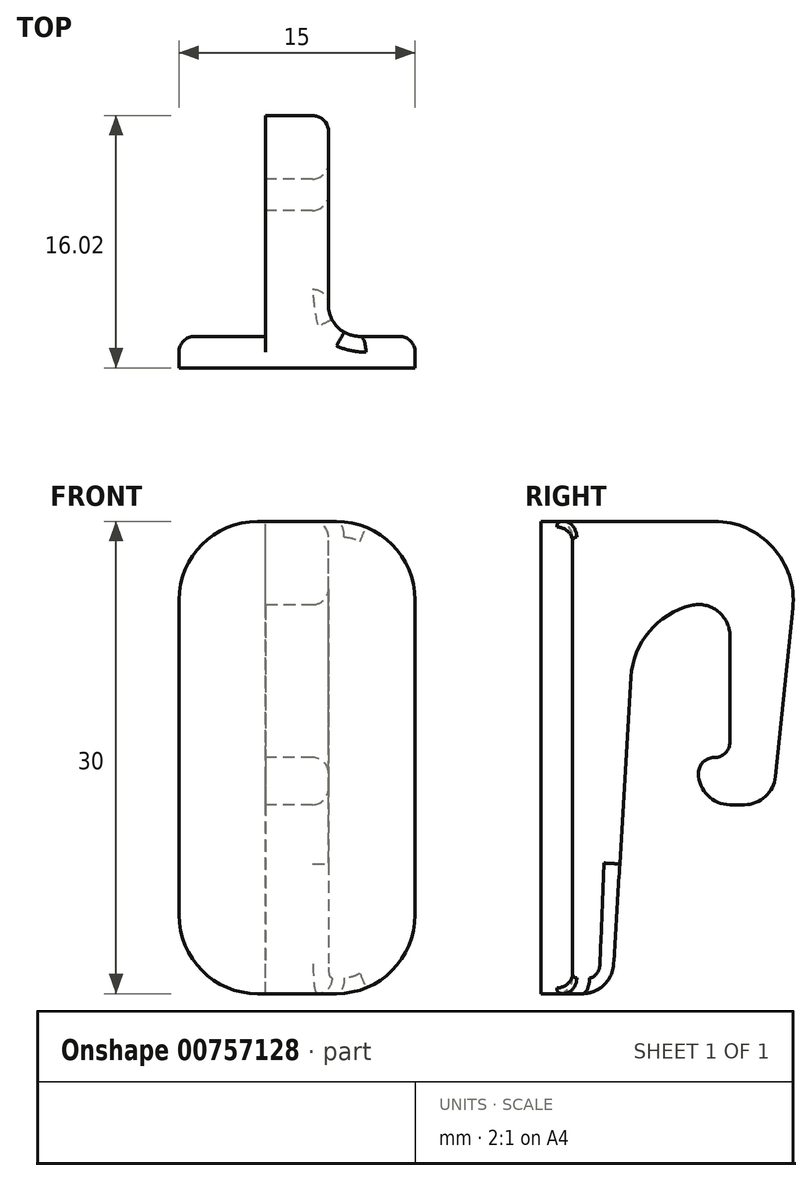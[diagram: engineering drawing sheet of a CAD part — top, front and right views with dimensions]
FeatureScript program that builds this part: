
annotation { "Feature Type Name" : "Feature", "Feature Type Description" : "" }
export const myFeature = defineFeature(function(context is Context, id is Id, definition is map)
    precondition{}
    {
        {
            var Q0;
            Q0=qCreatedBy(makeId("Right.planeOp"),FACE);
            var sketch = newSketch(context, id + "F0", { "sketchPlane" : qUnion([Q0])});
            skLineSegment(sketch, "E0", {"start": v(0, 0) * mm, "end": v(0, 30) * mm});
            skLineSegment(sketch, "E1", {"start": v(0, 30) * mm, "end": v(14.55, 30) * mm});
            skLineSegment(sketch, "E2", {"start": v(14.55, 30) * mm, "end": v(12.7, 12) * mm});
            skLineSegment(sketch, "E3", {"start": v(12.7, 12) * mm, "end": v(8, 12) * mm});
            skLineSegment(sketch, "E4", {"start": v(8, 12) * mm, "end": v(8, 15) * mm});
            skLineSegment(sketch, "E5", {"start": v(8, 15) * mm, "end": v(10, 15) * mm});
            skLineSegment(sketch, "E6", {"start": v(10, 15) * mm, "end": v(10, 24.8) * mm});
            skLineSegment(sketch, "E7", {"start": v(10, 24.8) * mm, "end": v(4, 24.8) * mm});
            skLineSegment(sketch, "E8", {"start": v(4, 24.8) * mm, "end": v(2.5, 0) * mm});
            skLineSegment(sketch, "E9", {"start": v(2.5, 0) * mm, "end": v(0, 0) * mm});
            skSolve(sketch);
        }
        {
            var Q0;
            Q0=makeQuery(id+"F0.imprint","IMPRINT",FACE,{"disambiguationData":[TD([[makeQuery(id+"F0.imprint","IMPRINT",EDGE,{"derivedFrom":sQuery(id+"F0.wireOp",EDGE,"E0")}),-1.0]])]});
            extrude(context, id + "F1", {"entities" : qUnion([Q0]), "endBound" : BoundingType.SYMMETRIC, "depth" : 4 * mm, "offsetDistance" : 25 * mm});
        }
        {
            var Q0;
            Q0=qCreatedBy(makeId("Front.planeOp"),FACE);
            var sketch = newSketch(context, id + "F2", { "sketchPlane" : qUnion([Q0])});
            skLineSegment(sketch, "E10.bottom", {"start": v(-7.5, 30) * mm, "end": v(7.5, 30) * mm});
            skLineSegment(sketch, "E10.top", {"start": v(-7.5, 0) * mm, "end": v(7.5, 0) * mm});
            skLineSegment(sketch, "E10.left", {"start": v(-7.5, 30) * mm, "end": v(-7.5, 0) * mm});
            skLineSegment(sketch, "E10.right", {"start": v(7.5, 30) * mm, "end": v(7.5, 0) * mm});
            skPoint(sketch, "E10.middle", {"position": v(0, 15) * mm});
            skSolve(sketch);
        }
        {
            var Q0;
            Q0 = qSketchRegion(id + "F2", true);
            extrude(context, id + "F3", {"entities" : qUnion([Q0]), "operationType" : NewBodyOperationType.ADD, "depth" : 2 * mm, "offsetDistance" : 25 * mm});
        }
        {
            var Q0;
            Q0=makeQuery(id+"F3.opExtrude","SWEPT_EDGE",EDGE,{"disambiguationData":[OSD([sQuery(id+"F2.wireOp",EDGE,"E10.bottom"),sQuery(id+"F2.wireOp",EDGE,"E10.right")])]});
            var Q1;
            Q1=makeQuery(id+"F3.opExtrude","SWEPT_EDGE",EDGE,{"disambiguationData":[OSD([sQuery(id+"F2.wireOp",EDGE,"E10.bottom"),sQuery(id+"F2.wireOp",EDGE,"E10.left")])]});
            var Q2;
            Q2=makeQuery(id+"F3.opExtrude","SWEPT_EDGE",EDGE,{"disambiguationData":[OSD([sQuery(id+"F2.wireOp",EDGE,"E10.top"),sQuery(id+"F2.wireOp",EDGE,"E10.right")])]});
            var Q3;
            Q3=makeQuery(id+"F1.opExtrude","SWEPT_EDGE",EDGE,{"disambiguationData":[OSD([sQuery(id+"F0.wireOp",EDGE,"E1"),sQuery(id+"F0.wireOp",EDGE,"E2")])]});
            var Q4;
            Q4=makeQuery(id+"F3.opExtrude","SWEPT_EDGE",EDGE,{"disambiguationData":[OSD([sQuery(id+"F2.wireOp",EDGE,"E10.top"),sQuery(id+"F2.wireOp",EDGE,"E10.left")])]});
            var Q5;
            Q5=makeQuery(id+"F1.opExtrude","SWEPT_EDGE",EDGE,{"disambiguationData":[OSD([sQuery(id+"F0.wireOp",EDGE,"E7"),sQuery(id+"F0.wireOp",EDGE,"E8")])]});
            fillet(context, id + "F4", {"entities" : qUnion([Q0, Q1, Q2, Q3, Q4, Q5]), "radius" : 5 * mm, "tangentPropagation" : true, "allowEdgeOverflow" : false});
        }
        {
            var Q0;
            Q0=makeQuery(id+"F1.opExtrude","SWEPT_EDGE",EDGE,{"disambiguationData":[OSD([sQuery(id+"F0.wireOp",EDGE,"E6"),sQuery(id+"F0.wireOp",EDGE,"E7")])]});
            var Q1;
            Q1=makeQuery(id+"F1.opExtrude","SWEPT_EDGE",EDGE,{"disambiguationData":[OSD([sQuery(id+"F0.wireOp",EDGE,"E3"),sQuery(id+"F0.wireOp",EDGE,"E4")])]});
            var Q2;
            Q2=makeQuery(id+"F1.opExtrude","SWEPT_EDGE",EDGE,{"disambiguationData":[OSD([sQuery(id+"F0.wireOp",EDGE,"E2"),sQuery(id+"F0.wireOp",EDGE,"E3")])]});
            var Q3;
            Q3=makeQuery(id+"F1.opExtrude","SWEPT_EDGE",EDGE,{"disambiguationData":[OSD([sQuery(id+"F0.wireOp",EDGE,"E8"),sQuery(id+"F0.wireOp",EDGE,"E9")])]});
            fillet(context, id + "F5", {"entities" : qUnion([Q0, Q1, Q2, Q3]), "radius" : 2 * mm, "tangentPropagation" : true, "allowEdgeOverflow" : false});
        }
        {
            var Q0;
            Q0=makeQuery(id+"F1.opExtrude","CAP_EDGE",EDGE,{"disambiguationData":[OSD([sQuery(id+"F0.wireOp",EDGE,"E0")])],"isStart":false});
            var Q1;
            Q1=makeQuery(id+"F1.opExtrude","CAP_EDGE",EDGE,{"disambiguationData":[OSD([sQuery(id+"F0.wireOp",EDGE,"E0")])],"isStart":true});
            fillet(context, id + "F6", {"entities" : qUnion([Q0, Q1]), "radius" : 2 * mm, "tangentPropagation" : true, "allowEdgeOverflow" : false});
        }
        {
            var Q0;
            Q0=makeQuery(id+"F1.opExtrude","SWEPT_EDGE",EDGE,{"disambiguationData":[OSD([sQuery(id+"F0.wireOp",EDGE,"E5"),sQuery(id+"F0.wireOp",EDGE,"E6")])]});
            var Q1;
            Q1=makeQuery(id+"F1.opExtrude","SWEPT_EDGE",EDGE,{"disambiguationData":[OSD([sQuery(id+"F0.wireOp",EDGE,"E4"),sQuery(id+"F0.wireOp",EDGE,"E5")])]});
            fillet(context, id + "F7", {"entities" : qUnion([Q0, Q1]), "radius" : 1 * mm, "tangentPropagation" : true, "allowEdgeOverflow" : false});
        }
        {
            var Q0;
            Q0=makeQuery(id+"F3.opExtrude","CAP_EDGE",EDGE,{"disambiguationData":[OSD([sQuery(id+"F2.wireOp",EDGE,"E10.right")])],"isStart":true});
            var Q1;
            Q1=makeQuery(id+"F3.opExtrude","CAP_EDGE",EDGE,{"disambiguationData":[OSD([sQuery(id+"F2.wireOp",EDGE,"E10.left")])],"isStart":true});
            fillet(context, id + "F8", {"entities" : qUnion([Q0, Q1]), "radius" : 1 * mm, "tangentPropagation" : true, "allowEdgeOverflow" : false});
        }
    });
